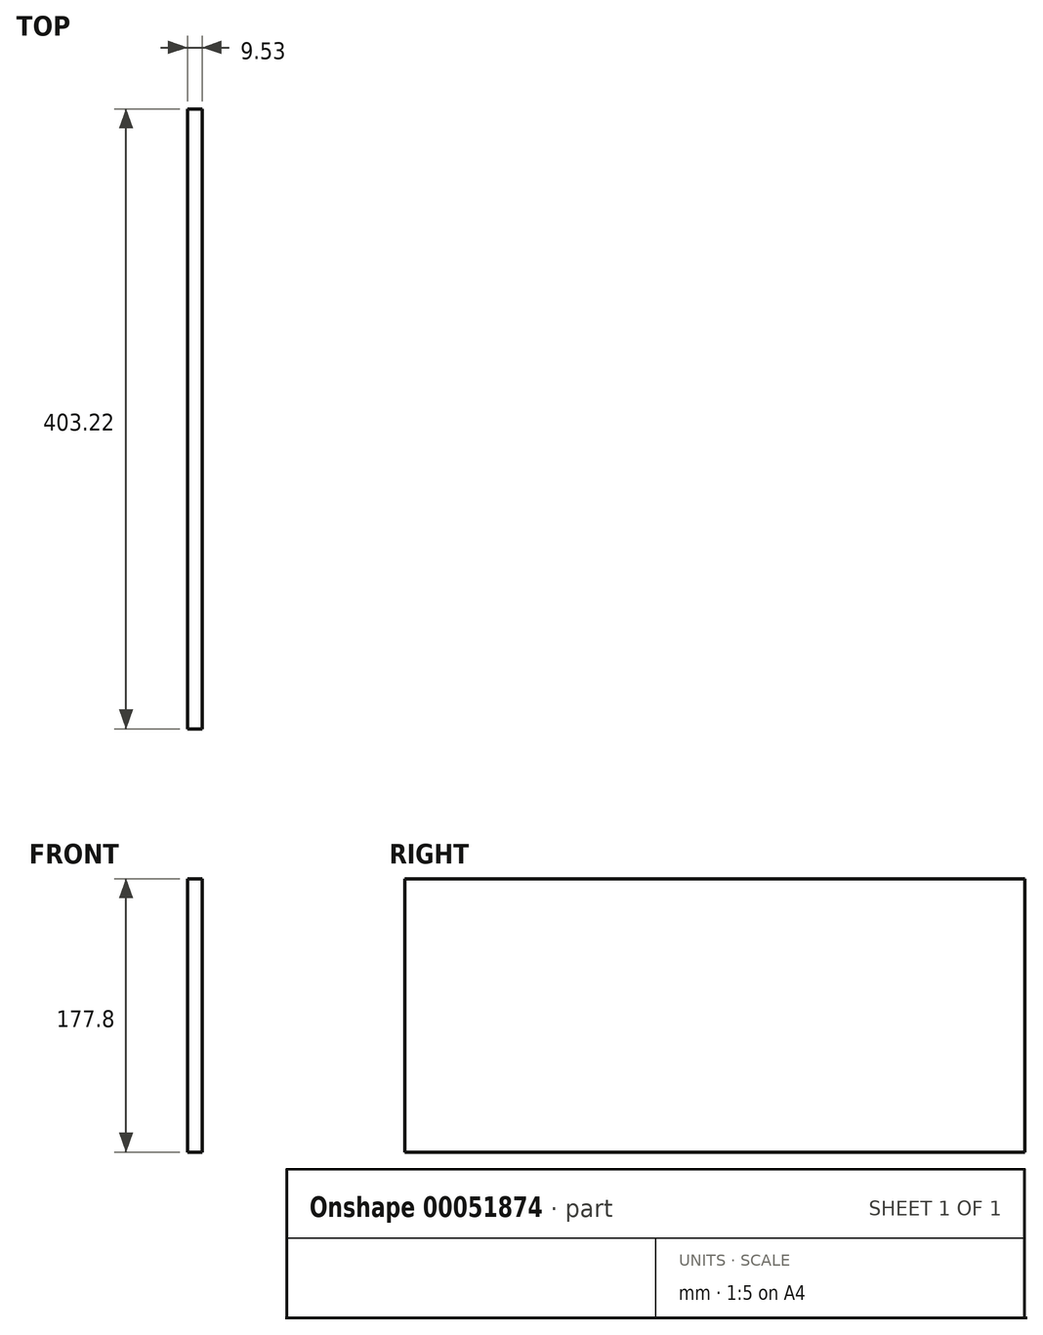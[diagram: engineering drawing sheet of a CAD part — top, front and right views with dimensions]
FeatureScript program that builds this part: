
annotation { "Feature Type Name" : "Feature", "Feature Type Description" : "" }
export const myFeature = defineFeature(function(context is Context, id is Id, definition is map)
    precondition{}
    {
        {
            var Q0;
            Q0=qCreatedBy(makeId("Right.planeOp"),FACE);
            var sketch = newSketch(context, id + "F0", { "sketchPlane" : qUnion([Q0])});
            skLineSegment(sketch, "E0.bottom", {"start": v(-177.8, 101.6) * mm, "end": v(225.43, 101.6) * mm});
            skLineSegment(sketch, "E0.top", {"start": v(-177.8, -76.2) * mm, "end": v(225.43, -76.2) * mm});
            skLineSegment(sketch, "E0.left", {"start": v(-177.8, 101.6) * mm, "end": v(-177.8, -76.2) * mm});
            skLineSegment(sketch, "E0.right", {"start": v(225.43, 101.6) * mm, "end": v(225.43, -76.2) * mm});
            skSolve(sketch);
        }
        {
            var Q0;
            Q0=makeQuery(id+"F0.imprint","IMPRINT",FACE,{"disambiguationData":[TD([[makeQuery(id+"F0.imprint","IMPRINT",EDGE,{"derivedFrom":sQuery(id+"F0.wireOp",EDGE,"E0.bottom")}),-1.0]])]});
            extrude(context, id + "F1", {"entities" : qUnion([Q0]), "depth" : 9.52 * mm});
        }
    });
